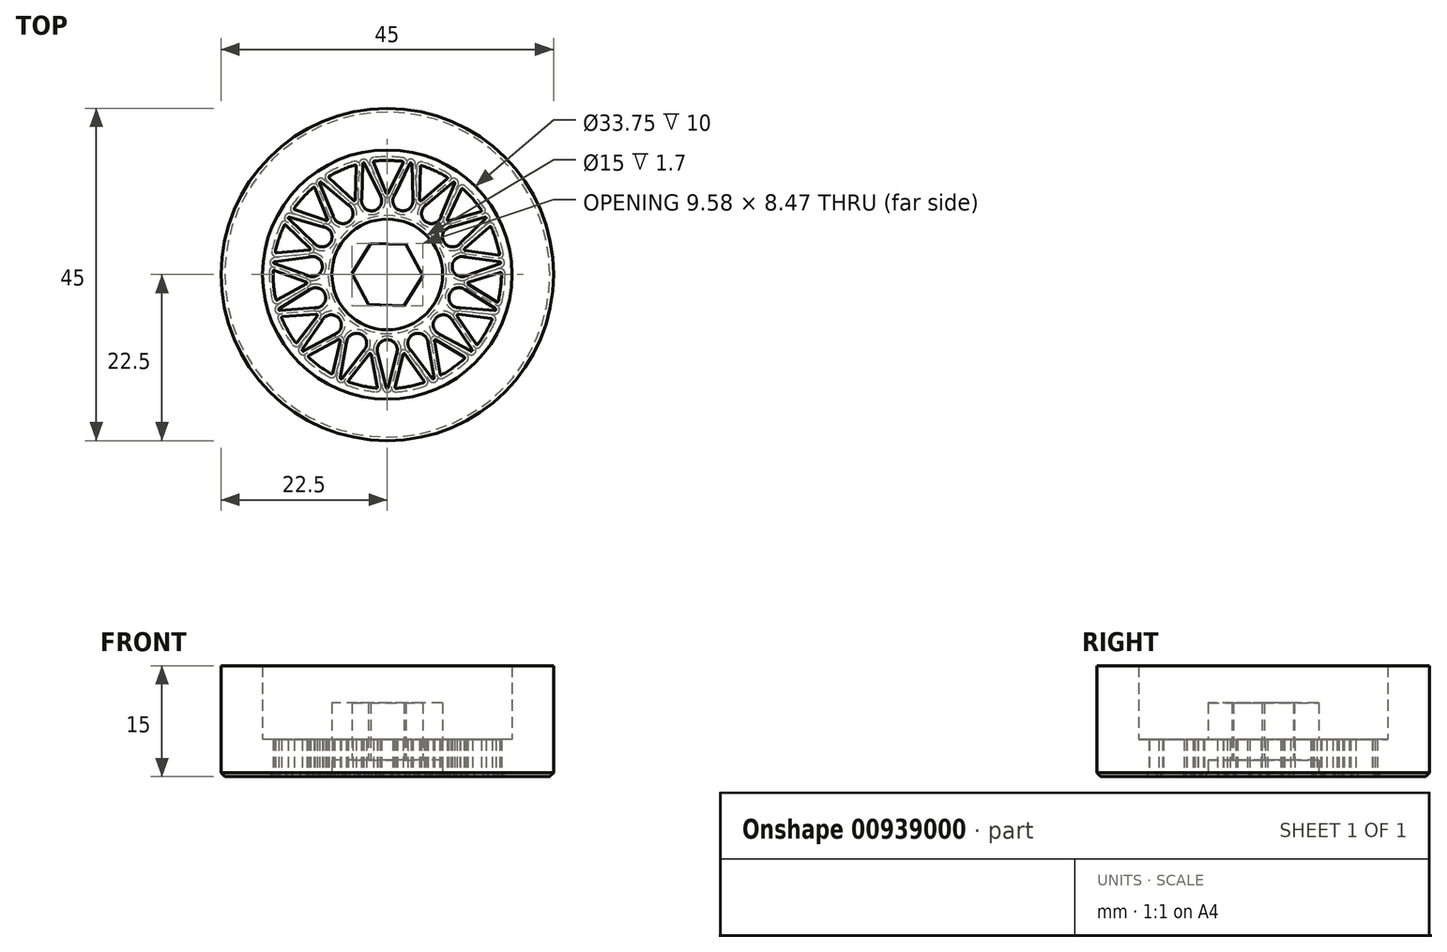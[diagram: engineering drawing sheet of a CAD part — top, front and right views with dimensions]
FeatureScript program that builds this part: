
annotation { "Feature Type Name" : "Feature", "Feature Type Description" : "" }
export const myFeature = defineFeature(function(context is Context, id is Id, definition is map)
    precondition{}
    {
        {
            var Q0;
            Q0=qCreatedBy(makeId("Top.planeOp"),FACE);
            var sketch = newSketch(context, id + "F0", { "sketchPlane" : qUnion([Q0])});
            skCircle(sketch, "E0", {"center": v(0, 0) * mm, "radius": 22.5 * mm});
            skCircle(sketch, "E1", {"center": v(0, 0) * mm, "radius": 16.88 * mm});
            skCircle(sketch, "E2", {"center": v(0, 0) * mm, "radius": 7.5 * mm});
            skCircle(sketch, "E3", {"center": v(0, 0) * mm, "radius": 15.9 * mm, "construction": true});
            skCircle(sketch, "E4", {"center": v(0, 0) * mm, "radius": 5.66 * mm, "construction": true});
            skLineSegment(sketch, "E5", {"start": v(0, -5.66) * mm, "end": v(0, -15.9) * mm, "construction": true});
            skArc(sketch, "E6", {"start": v(1.26, -10.71) * mm, "mid": v(0, -8.84) * mm, "end": v(-1.26, -10.71) * mm});
            skLineSegment(sketch, "E7", {"start": v(-1.26, -10.71) * mm, "end": v(-0.14, -15.34) * mm});
            skLineSegment(sketch, "E8", {"start": v(0.14, -15.34) * mm, "end": v(1.26, -10.71) * mm});
            skPoint(sketch, "E9.visualSharp", {"position": v(0, -15.9) * mm});
            skArc(sketch, "E9.filletArc", {"start": v(-0.14, -15.34) * mm, "mid": v(0, -15.44) * mm, "end": v(0.14, -15.34) * mm});
            skArc(sketch, "E10.1.0", {"start": v(5.51, -9.27) * mm, "mid": v(3.6, -8.07) * mm, "end": v(3.2, -10.3) * mm});
            skLineSegment(sketch, "E10.1.1", {"start": v(6.36, -13.95) * mm, "end": v(5.51, -9.27) * mm});
            skLineSegment(sketch, "E10.1.2", {"start": v(3.2, -10.3) * mm, "end": v(6.11, -14.07) * mm});
            skArc(sketch, "E10.1.3", {"start": v(6.11, -14.07) * mm, "mid": v(6.28, -14.1) * mm, "end": v(6.36, -13.95) * mm});
            skArc(sketch, "E10.2.0", {"start": v(8.8, -6.23) * mm, "mid": v(6.57, -5.91) * mm, "end": v(7.12, -8.1) * mm});
            skLineSegment(sketch, "E10.2.1", {"start": v(11.49, -10.16) * mm, "end": v(8.8, -6.23) * mm});
            skLineSegment(sketch, "E10.2.2", {"start": v(7.12, -8.1) * mm, "end": v(11.3, -10.36) * mm});
            skArc(sketch, "E10.2.3", {"start": v(11.3, -10.36) * mm, "mid": v(11.48, -10.33) * mm, "end": v(11.49, -10.16) * mm});
            skArc(sketch, "E10.3.0", {"start": v(10.58, -2.1) * mm, "mid": v(8.4, -2.73) * mm, "end": v(9.8, -4.51) * mm});
            skLineSegment(sketch, "E10.3.1", {"start": v(14.63, -4.6) * mm, "end": v(10.58, -2.1) * mm});
            skLineSegment(sketch, "E10.3.2", {"start": v(9.8, -4.51) * mm, "end": v(14.54, -4.87) * mm});
            skArc(sketch, "E10.3.3", {"start": v(14.54, -4.87) * mm, "mid": v(14.69, -4.77) * mm, "end": v(14.63, -4.6) * mm});
            skArc(sketch, "E10.4.0", {"start": v(10.52, 2.38) * mm, "mid": v(8.79, 0.92) * mm, "end": v(10.79, -0.14) * mm});
            skLineSegment(sketch, "E10.4.1", {"start": v(15.24, 1.74) * mm, "end": v(10.52, 2.38) * mm});
            skLineSegment(sketch, "E10.4.2", {"start": v(10.79, -0.14) * mm, "end": v(15.27, 1.47) * mm});
            skArc(sketch, "E10.4.3", {"start": v(15.27, 1.47) * mm, "mid": v(15.36, 1.61) * mm, "end": v(15.24, 1.74) * mm});
            skArc(sketch, "E10.5.0", {"start": v(8.65, 6.45) * mm, "mid": v(7.65, 4.42) * mm, "end": v(9.9, 4.26) * mm});
            skLineSegment(sketch, "E10.5.1", {"start": v(13.21, 7.79) * mm, "end": v(8.65, 6.45) * mm});
            skLineSegment(sketch, "E10.5.2", {"start": v(9.9, 4.26) * mm, "end": v(13.35, 7.55) * mm});
            skArc(sketch, "E10.5.3", {"start": v(13.35, 7.55) * mm, "mid": v(13.38, 7.72) * mm, "end": v(13.21, 7.79) * mm});
            skArc(sketch, "E10.6.0", {"start": v(5.27, 9.4) * mm, "mid": v(5.2, 7.15) * mm, "end": v(7.32, 7.92) * mm});
            skLineSegment(sketch, "E10.6.1", {"start": v(8.9, 12.49) * mm, "end": v(5.27, 9.4) * mm});
            skLineSegment(sketch, "E10.6.2", {"start": v(7.32, 7.92) * mm, "end": v(9.13, 12.33) * mm});
            skArc(sketch, "E10.6.3", {"start": v(9.13, 12.33) * mm, "mid": v(9.08, 12.5) * mm, "end": v(8.9, 12.49) * mm});
            skArc(sketch, "E10.7.0", {"start": v(1, 10.74) * mm, "mid": v(1.84, 8.64) * mm, "end": v(3.46, 10.22) * mm});
            skLineSegment(sketch, "E10.7.1", {"start": v(3.05, 15.03) * mm, "end": v(1, 10.74) * mm});
            skLineSegment(sketch, "E10.7.2", {"start": v(3.46, 10.22) * mm, "end": v(3.32, 14.97) * mm});
            skArc(sketch, "E10.7.3", {"start": v(3.32, 14.97) * mm, "mid": v(3.21, 15.1) * mm, "end": v(3.05, 15.03) * mm});
            skArc(sketch, "E10.8.0", {"start": v(-3.46, 10.22) * mm, "mid": v(-1.84, 8.64) * mm, "end": v(-1, 10.74) * mm});
            skLineSegment(sketch, "E10.8.1", {"start": v(-3.32, 14.97) * mm, "end": v(-3.46, 10.22) * mm});
            skLineSegment(sketch, "E10.8.2", {"start": v(-1, 10.74) * mm, "end": v(-3.05, 15.03) * mm});
            skArc(sketch, "E10.8.3", {"start": v(-3.05, 15.03) * mm, "mid": v(-3.21, 15.1) * mm, "end": v(-3.32, 14.97) * mm});
            skArc(sketch, "E10.9.0", {"start": v(-7.32, 7.92) * mm, "mid": v(-5.2, 7.15) * mm, "end": v(-5.27, 9.4) * mm});
            skLineSegment(sketch, "E10.9.1", {"start": v(-9.13, 12.33) * mm, "end": v(-7.32, 7.92) * mm});
            skLineSegment(sketch, "E10.9.2", {"start": v(-5.27, 9.4) * mm, "end": v(-8.9, 12.49) * mm});
            skArc(sketch, "E10.9.3", {"start": v(-8.9, 12.49) * mm, "mid": v(-9.08, 12.5) * mm, "end": v(-9.13, 12.33) * mm});
            skArc(sketch, "E10.10.0", {"start": v(-9.9, 4.26) * mm, "mid": v(-7.65, 4.42) * mm, "end": v(-8.65, 6.45) * mm});
            skLineSegment(sketch, "E10.10.1", {"start": v(-13.35, 7.55) * mm, "end": v(-9.9, 4.26) * mm});
            skLineSegment(sketch, "E10.10.2", {"start": v(-8.65, 6.45) * mm, "end": v(-13.21, 7.79) * mm});
            skArc(sketch, "E10.10.3", {"start": v(-13.21, 7.79) * mm, "mid": v(-13.38, 7.72) * mm, "end": v(-13.35, 7.55) * mm});
            skArc(sketch, "E10.11.0", {"start": v(-10.79, -0.14) * mm, "mid": v(-8.79, 0.92) * mm, "end": v(-10.52, 2.38) * mm});
            skLineSegment(sketch, "E10.11.1", {"start": v(-15.27, 1.47) * mm, "end": v(-10.79, -0.14) * mm});
            skLineSegment(sketch, "E10.11.2", {"start": v(-10.52, 2.38) * mm, "end": v(-15.24, 1.74) * mm});
            skArc(sketch, "E10.11.3", {"start": v(-15.24, 1.74) * mm, "mid": v(-15.36, 1.61) * mm, "end": v(-15.27, 1.47) * mm});
            skArc(sketch, "E10.12.0", {"start": v(-9.8, -4.51) * mm, "mid": v(-8.4, -2.73) * mm, "end": v(-10.58, -2.1) * mm});
            skLineSegment(sketch, "E10.12.1", {"start": v(-14.54, -4.87) * mm, "end": v(-9.8, -4.51) * mm});
            skLineSegment(sketch, "E10.12.2", {"start": v(-10.58, -2.1) * mm, "end": v(-14.63, -4.6) * mm});
            skArc(sketch, "E10.12.3", {"start": v(-14.63, -4.6) * mm, "mid": v(-14.69, -4.77) * mm, "end": v(-14.54, -4.87) * mm});
            skArc(sketch, "E10.13.0", {"start": v(-7.12, -8.1) * mm, "mid": v(-6.57, -5.91) * mm, "end": v(-8.8, -6.23) * mm});
            skLineSegment(sketch, "E10.13.1", {"start": v(-11.3, -10.36) * mm, "end": v(-7.12, -8.1) * mm});
            skLineSegment(sketch, "E10.13.2", {"start": v(-8.8, -6.23) * mm, "end": v(-11.49, -10.16) * mm});
            skArc(sketch, "E10.13.3", {"start": v(-11.49, -10.16) * mm, "mid": v(-11.48, -10.33) * mm, "end": v(-11.3, -10.36) * mm});
            skArc(sketch, "E10.14.0", {"start": v(-3.2, -10.3) * mm, "mid": v(-3.6, -8.07) * mm, "end": v(-5.51, -9.27) * mm});
            skLineSegment(sketch, "E10.14.1", {"start": v(-6.11, -14.07) * mm, "end": v(-3.2, -10.3) * mm});
            skLineSegment(sketch, "E10.14.2", {"start": v(-5.51, -9.27) * mm, "end": v(-6.36, -13.95) * mm});
            skArc(sketch, "E10.14.3", {"start": v(-6.36, -13.95) * mm, "mid": v(-6.28, -14.1) * mm, "end": v(-6.11, -14.07) * mm});
            skCircle(sketch, "E11", {"center": v(0, 0) * mm, "radius": 15.46 * mm, "construction": true});
            skPoint(sketch, "E12", {"position": v(-5.37, -14.5) * mm});
            skPoint(sketch, "E13", {"position": v(-1.3, -15.4) * mm});
            skArc(sketch, "E14", {"start": v(-5.18, -14.57) * mm, "mid": v(-3.35, -15.08) * mm, "end": v(-1.48, -15.39) * mm});
            skLineSegment(sketch, "E15", {"start": v(-3.2, -10.3) * mm, "end": v(-1.26, -10.71) * mm, "construction": true});
            skLineSegment(sketch, "E16", {"start": v(-5.25, -14.34) * mm, "end": v(-2.43, -10.75) * mm});
            skLineSegment(sketch, "E17", {"start": v(-2.17, -10.81) * mm, "end": v(-1.33, -15.22) * mm});
            skArc(sketch, "E18.filletArc", {"start": v(-5.25, -14.34) * mm, "mid": v(-5.27, -14.47) * mm, "end": v(-5.18, -14.57) * mm});
            skArc(sketch, "E19.filletArc", {"start": v(-1.48, -15.39) * mm, "mid": v(-1.36, -15.34) * mm, "end": v(-1.33, -15.22) * mm});
            skPoint(sketch, "E20.visualSharp", {"position": v(-2.23, -10.5) * mm});
            skArc(sketch, "E20.filletArc", {"start": v(-2.17, -10.81) * mm, "mid": v(-2.28, -10.7) * mm, "end": v(-2.43, -10.75) * mm});
            skArc(sketch, "E21.1.0", {"start": v(1.2, -15.41) * mm, "mid": v(3.07, -15.14) * mm, "end": v(4.9, -14.66) * mm});
            skLineSegment(sketch, "E21.1.1", {"start": v(2.41, -10.76) * mm, "end": v(4.98, -14.44) * mm});
            skLineSegment(sketch, "E21.1.2", {"start": v(1.04, -15.24) * mm, "end": v(2.16, -10.8) * mm});
            skArc(sketch, "E21.1.3", {"start": v(2.41, -10.76) * mm, "mid": v(2.27, -10.7) * mm, "end": v(2.16, -10.8) * mm});
            skArc(sketch, "E21.1.4", {"start": v(4.9, -14.66) * mm, "mid": v(5, -14.57) * mm, "end": v(4.98, -14.44) * mm});
            skArc(sketch, "E21.1.5", {"start": v(1.04, -15.24) * mm, "mid": v(1.07, -15.36) * mm, "end": v(1.2, -15.41) * mm});
            skArc(sketch, "E21.2.0", {"start": v(7.36, -13.6) * mm, "mid": v(8.96, -12.58) * mm, "end": v(10.45, -11.4) * mm});
            skLineSegment(sketch, "E21.2.1", {"start": v(6.58, -8.85) * mm, "end": v(10.42, -11.17) * mm});
            skLineSegment(sketch, "E21.2.2", {"start": v(7.15, -13.5) * mm, "end": v(6.37, -9) * mm});
            skArc(sketch, "E21.2.3", {"start": v(6.58, -8.85) * mm, "mid": v(6.43, -8.86) * mm, "end": v(6.37, -9) * mm});
            skArc(sketch, "E21.2.4", {"start": v(10.45, -11.4) * mm, "mid": v(10.5, -11.28) * mm, "end": v(10.42, -11.17) * mm});
            skArc(sketch, "E21.2.5", {"start": v(7.15, -13.5) * mm, "mid": v(7.23, -13.6) * mm, "end": v(7.36, -13.6) * mm});
            skArc(sketch, "E21.3.0", {"start": v(12.25, -9.43) * mm, "mid": v(13.3, -7.85) * mm, "end": v(14.18, -6.16) * mm});
            skLineSegment(sketch, "E21.3.1", {"start": v(9.61, -5.4) * mm, "end": v(14.07, -5.96) * mm});
            skLineSegment(sketch, "E21.3.2", {"start": v(12.02, -9.42) * mm, "end": v(9.48, -5.63) * mm});
            skArc(sketch, "E21.3.3", {"start": v(9.61, -5.4) * mm, "mid": v(9.47, -5.48) * mm, "end": v(9.48, -5.63) * mm});
            skArc(sketch, "E21.3.4", {"start": v(14.18, -6.16) * mm, "mid": v(14.17, -6.04) * mm, "end": v(14.07, -5.96) * mm});
            skArc(sketch, "E21.3.5", {"start": v(12.02, -9.42) * mm, "mid": v(12.14, -9.48) * mm, "end": v(12.25, -9.43) * mm});
            skArc(sketch, "E21.4.0", {"start": v(15.03, -3.63) * mm, "mid": v(15.35, -1.76) * mm, "end": v(15.46, 0.14) * mm});
            skLineSegment(sketch, "E21.4.1", {"start": v(10.98, -1.03) * mm, "end": v(15.28, 0.27) * mm});
            skLineSegment(sketch, "E21.4.2", {"start": v(14.81, -3.72) * mm, "end": v(10.95, -1.29) * mm});
            skArc(sketch, "E21.4.3", {"start": v(10.98, -1.03) * mm, "mid": v(10.88, -1.15) * mm, "end": v(10.95, -1.29) * mm});
            skArc(sketch, "E21.4.4", {"start": v(15.46, 0.14) * mm, "mid": v(15.4, 0.25) * mm, "end": v(15.28, 0.27) * mm});
            skArc(sketch, "E21.4.5", {"start": v(14.81, -3.72) * mm, "mid": v(14.94, -3.73) * mm, "end": v(15.03, -3.63) * mm});
            skArc(sketch, "E21.5.0", {"start": v(15.2, 2.8) * mm, "mid": v(14.74, 4.64) * mm, "end": v(14.07, 6.41) * mm});
            skLineSegment(sketch, "E21.5.1", {"start": v(10.45, 3.52) * mm, "end": v(13.84, 6.46) * mm});
            skLineSegment(sketch, "E21.5.2", {"start": v(15.05, 2.63) * mm, "end": v(10.52, 3.28) * mm});
            skArc(sketch, "E21.5.3", {"start": v(10.45, 3.52) * mm, "mid": v(10.4, 3.38) * mm, "end": v(10.52, 3.28) * mm});
            skArc(sketch, "E21.5.4", {"start": v(14.07, 6.41) * mm, "mid": v(13.97, 6.5) * mm, "end": v(13.84, 6.46) * mm});
            skArc(sketch, "E21.5.5", {"start": v(15.05, 2.63) * mm, "mid": v(15.17, 2.67) * mm, "end": v(15.2, 2.8) * mm});
            skArc(sketch, "E21.6.0", {"start": v(12.75, 8.74) * mm, "mid": v(11.58, 10.23) * mm, "end": v(10.24, 11.58) * mm});
            skLineSegment(sketch, "E21.6.1", {"start": v(8.11, 7.47) * mm, "end": v(10.02, 11.53) * mm});
            skLineSegment(sketch, "E21.6.2", {"start": v(12.68, 8.52) * mm, "end": v(8.28, 7.27) * mm});
            skArc(sketch, "E21.6.3", {"start": v(8.11, 7.47) * mm, "mid": v(8.13, 7.32) * mm, "end": v(8.28, 7.27) * mm});
            skArc(sketch, "E21.6.4", {"start": v(10.24, 11.58) * mm, "mid": v(10.12, 11.61) * mm, "end": v(10.02, 11.53) * mm});
            skArc(sketch, "E21.6.5", {"start": v(12.68, 8.52) * mm, "mid": v(12.77, 8.61) * mm, "end": v(12.75, 8.74) * mm});
            skArc(sketch, "E21.7.0", {"start": v(8.1, 13.17) * mm, "mid": v(6.42, 14.06) * mm, "end": v(4.65, 14.75) * mm});
            skLineSegment(sketch, "E21.7.1", {"start": v(4.37, 10.12) * mm, "end": v(4.46, 14.61) * mm});
            skLineSegment(sketch, "E21.7.2", {"start": v(8.11, 12.94) * mm, "end": v(4.6, 10.01) * mm});
            skArc(sketch, "E21.7.3", {"start": v(4.37, 10.12) * mm, "mid": v(4.46, 10) * mm, "end": v(4.6, 10.01) * mm});
            skArc(sketch, "E21.7.4", {"start": v(4.65, 14.75) * mm, "mid": v(4.52, 14.73) * mm, "end": v(4.46, 14.61) * mm});
            skArc(sketch, "E21.7.5", {"start": v(8.11, 12.94) * mm, "mid": v(8.16, 13.06) * mm, "end": v(8.1, 13.17) * mm});
            skArc(sketch, "E21.8.0", {"start": v(2.04, 15.33) * mm, "mid": v(0.14, 15.45) * mm, "end": v(-1.75, 15.36) * mm});
            skLineSegment(sketch, "E21.8.1", {"start": v(-0.12, 11.03) * mm, "end": v(-1.87, 15.16) * mm});
            skLineSegment(sketch, "E21.8.2", {"start": v(2.15, 15.12) * mm, "end": v(0.14, 11.02) * mm});
            skArc(sketch, "E21.8.3", {"start": v(-0.12, 11.03) * mm, "mid": v(0, 10.94) * mm, "end": v(0.14, 11.02) * mm});
            skArc(sketch, "E21.8.4", {"start": v(-1.75, 15.36) * mm, "mid": v(-1.86, 15.3) * mm, "end": v(-1.87, 15.16) * mm});
            skArc(sketch, "E21.8.5", {"start": v(2.15, 15.12) * mm, "mid": v(2.15, 15.25) * mm, "end": v(2.04, 15.33) * mm});
            skArc(sketch, "E21.9.0", {"start": v(-4.37, 14.83) * mm, "mid": v(-6.15, 14.17) * mm, "end": v(-7.85, 13.32) * mm});
            skLineSegment(sketch, "E21.9.1", {"start": v(-4.6, 10.03) * mm, "end": v(-7.87, 13.1) * mm});
            skLineSegment(sketch, "E21.9.2", {"start": v(-4.19, 14.69) * mm, "end": v(-4.36, 10.12) * mm});
            skArc(sketch, "E21.9.3", {"start": v(-4.6, 10.03) * mm, "mid": v(-4.45, 10) * mm, "end": v(-4.36, 10.12) * mm});
            skArc(sketch, "E21.9.4", {"start": v(-7.85, 13.32) * mm, "mid": v(-7.92, 13.21) * mm, "end": v(-7.87, 13.1) * mm});
            skArc(sketch, "E21.9.5", {"start": v(-4.19, 14.69) * mm, "mid": v(-4.24, 14.8) * mm, "end": v(-4.37, 14.83) * mm});
            skArc(sketch, "E21.10.0", {"start": v(-10.03, 11.77) * mm, "mid": v(-11.38, 10.45) * mm, "end": v(-12.59, 8.98) * mm});
            skLineSegment(sketch, "E21.10.1", {"start": v(-8.28, 7.29) * mm, "end": v(-12.52, 8.76) * mm});
            skLineSegment(sketch, "E21.10.2", {"start": v(-9.8, 11.72) * mm, "end": v(-8.1, 7.48) * mm});
            skArc(sketch, "E21.10.3", {"start": v(-8.28, 7.29) * mm, "mid": v(-8.13, 7.33) * mm, "end": v(-8.1, 7.48) * mm});
            skArc(sketch, "E21.10.4", {"start": v(-12.59, 8.98) * mm, "mid": v(-12.6, 8.85) * mm, "end": v(-12.52, 8.76) * mm});
            skArc(sketch, "E21.10.5", {"start": v(-9.8, 11.72) * mm, "mid": v(-9.9, 11.8) * mm, "end": v(-10.03, 11.77) * mm});
            skArc(sketch, "E21.11.0", {"start": v(-13.95, 6.67) * mm, "mid": v(-14.65, 4.91) * mm, "end": v(-15.15, 3.08) * mm});
            skLineSegment(sketch, "E21.11.1", {"start": v(-10.53, 3.3) * mm, "end": v(-15, 2.9) * mm});
            skLineSegment(sketch, "E21.11.2", {"start": v(-13.72, 6.72) * mm, "end": v(-10.44, 3.54) * mm});
            skArc(sketch, "E21.11.3", {"start": v(-10.53, 3.3) * mm, "mid": v(-10.4, 3.39) * mm, "end": v(-10.44, 3.54) * mm});
            skArc(sketch, "E21.11.4", {"start": v(-15.15, 3.08) * mm, "mid": v(-15.12, 2.96) * mm, "end": v(-15, 2.9) * mm});
            skArc(sketch, "E21.11.5", {"start": v(-13.72, 6.72) * mm, "mid": v(-13.84, 6.75) * mm, "end": v(-13.95, 6.67) * mm});
            skArc(sketch, "E21.12.0", {"start": v(-15.45, 0.43) * mm, "mid": v(-15.38, -1.47) * mm, "end": v(-15.1, -3.35) * mm});
            skLineSegment(sketch, "E21.12.1", {"start": v(-10.96, -1.27) * mm, "end": v(-14.89, -3.44) * mm});
            skLineSegment(sketch, "E21.12.2", {"start": v(-15.26, 0.56) * mm, "end": v(-10.97, -1.02) * mm});
            skArc(sketch, "E21.12.3", {"start": v(-10.96, -1.27) * mm, "mid": v(-10.88, -1.14) * mm, "end": v(-10.97, -1.02) * mm});
            skArc(sketch, "E21.12.4", {"start": v(-15.1, -3.35) * mm, "mid": v(-15.01, -3.45) * mm, "end": v(-14.89, -3.44) * mm});
            skArc(sketch, "E21.12.5", {"start": v(-15.26, 0.56) * mm, "mid": v(-15.4, 0.54) * mm, "end": v(-15.45, 0.43) * mm});
            skArc(sketch, "E21.13.0", {"start": v(-14.3, -5.9) * mm, "mid": v(-13.45, -7.6) * mm, "end": v(-12.43, -9.2) * mm});
            skLineSegment(sketch, "E21.13.1", {"start": v(-9.5, -5.62) * mm, "end": v(-12.2, -9.2) * mm});
            skLineSegment(sketch, "E21.13.2", {"start": v(-14.17, -5.7) * mm, "end": v(-9.61, -5.4) * mm});
            skArc(sketch, "E21.13.3", {"start": v(-9.5, -5.62) * mm, "mid": v(-9.48, -5.47) * mm, "end": v(-9.61, -5.4) * mm});
            skArc(sketch, "E21.13.4", {"start": v(-12.43, -9.2) * mm, "mid": v(-12.31, -9.26) * mm, "end": v(-12.2, -9.2) * mm});
            skArc(sketch, "E21.13.5", {"start": v(-14.17, -5.7) * mm, "mid": v(-14.28, -5.77) * mm, "end": v(-14.3, -5.9) * mm});
            skArc(sketch, "E21.14.0", {"start": v(-10.66, -11.2) * mm, "mid": v(-9.2, -12.41) * mm, "end": v(-7.61, -13.46) * mm});
            skLineSegment(sketch, "E21.14.1", {"start": v(-6.38, -9) * mm, "end": v(-7.4, -13.37) * mm});
            skLineSegment(sketch, "E21.14.2", {"start": v(-10.63, -10.97) * mm, "end": v(-6.59, -8.84) * mm});
            skArc(sketch, "E21.14.3", {"start": v(-6.38, -9) * mm, "mid": v(-6.44, -8.85) * mm, "end": v(-6.59, -8.84) * mm});
            skArc(sketch, "E21.14.4", {"start": v(-7.61, -13.46) * mm, "mid": v(-7.48, -13.46) * mm, "end": v(-7.4, -13.37) * mm});
            skArc(sketch, "E21.14.5", {"start": v(-10.63, -10.97) * mm, "mid": v(-10.7, -11.08) * mm, "end": v(-10.66, -11.2) * mm});
            skSolve(sketch);
        }
        {
            var Q0;
            Q0=makeQuery(id+"F0.imprint","IMPRINT",FACE,{"disambiguationData":[TD([[makeQuery(id+"F0.imprint","IMPRINT",EDGE,{"derivedFrom":sQuery(id+"F0.wireOp",EDGE,"E0")}),1.0]])]});
            extrude(context, id + "F1", {"entities" : qUnion([Q0]), "depth" : 15 * mm, "offsetDistance" : 25 * mm});
        }
        {
            var Q0;
            Q0=makeQuery(id+"F0.imprint","IMPRINT",FACE,{"disambiguationData":[TD([[makeQuery(id+"F0.imprint","IMPRINT",EDGE,{"derivedFrom":sQuery(id+"F0.wireOp",EDGE,"E1")}),1.0]])]});
            extrude(context, id + "F2", {"entities" : qUnion([Q0]), "operationType" : NewBodyOperationType.ADD, "depth" : 5 * mm, "offsetDistance" : 25 * mm});
        }
        {
            var Q0;
            {var subQ0=sQuery(id+"F0.wireOp",EDGE,"E2");var subQ1=makeQuery(id+"F0.imprint","INTERSECT",VERTEX,{"derivedFrom":[subQ0,sQuery(id+"F0.wireOp",EDGE,"FMw9U3Ag-M4uU-eOUw-AIyu-Y3kzjyrUIhWa.right")]});Q0=makeQuery(id+"F0.imprint","IMPRINT",FACE,{"disambiguationData":[TD([[makeQuery(id+"F0.imprint","IMPRINT",EDGE,{"disambiguationData":[TD([[subQ1,1.0]])],"derivedFrom":subQ0}),1.0]])]});}
            extrude(context, id + "F3", {"entities" : qUnion([Q0]), "operationType" : NewBodyOperationType.ADD, "depth" : 10 * mm, "offsetDistance" : 25 * mm});
        }
        {
            var Q0;
            Q0=makeQuery(id+"F0.imprint","IMPRINT",FACE,{"disambiguationData":[TD([[makeQuery(id+"F0.imprint","IMPRINT",EDGE,{"derivedFrom":sQuery(id+"F0.wireOp",EDGE,"E2")}),1.0]])]});
            extrude(context, id + "F4", {"entities" : qUnion([Q0]), "operationType" : NewBodyOperationType.REMOVE, "depth" : 2.2 * mm, "offsetDistance" : 25 * mm});
        }
        {
            var Q0;
            Q0=makeQuery(id+"F0.imprint","IMPRINT",FACE,{"disambiguationData":[TD([[makeQuery(id+"F0.imprint","IMPRINT",EDGE,{"derivedFrom":sQuery(id+"F0.wireOp",EDGE,"E2")}),1.0]])]});
            var sketch = newSketch(context, id + "F5", { "sketchPlane" : qUnion([Q0])});
            skPoint(sketch, "E22.center", {"position": v(0, 0) * mm});
            skPoint(sketch, "E23.0.midPoint", {"position": v(-3.35, 1.99) * mm});
            skCircle(sketch, "E24.cCircle", {"center": v(0, 0) * mm, "radius": 4.15 * mm, "construction": true});
            skLineSegment(sketch, "E24.0", {"start": v(-4.79, 0.17) * mm, "end": v(-2.25, 4.23) * mm});
            skLineSegment(sketch, "E24.1", {"start": v(-2.25, 4.23) * mm, "end": v(2.54, 4.06) * mm});
            skLineSegment(sketch, "E24.2", {"start": v(2.54, 4.06) * mm, "end": v(4.79, -0.17) * mm});
            skLineSegment(sketch, "E24.3", {"start": v(4.79, -0.17) * mm, "end": v(2.25, -4.23) * mm});
            skLineSegment(sketch, "E24.4", {"start": v(2.25, -4.23) * mm, "end": v(-2.54, -4.06) * mm});
            skLineSegment(sketch, "E24.5", {"start": v(-2.54, -4.06) * mm, "end": v(-4.79, 0.17) * mm});
            skPoint(sketch, "E24.0.midPoint", {"position": v(-3.52, 2.2) * mm});
            skPoint(sketch, "E25.orphan", {"position": v(-2.3, -3.87) * mm});
            skPoint(sketch, "E26.orphan", {"position": v(2.2, -3.92) * mm});
            skPoint(sketch, "E27.orphan", {"position": v(-4.5, 0.05) * mm});
            skPoint(sketch, "E23.1.start.orphan", {"position": v(-2.2, 3.92) * mm});
            skSolve(sketch);
        }
        {
            var Q0;
            Q0=makeQuery(id+"F5.imprint","IMPRINT",FACE,{"disambiguationData":[TD([[makeQuery(id+"F5.imprint","IMPRINT",EDGE,{"derivedFrom":sQuery(id+"F5.wireOp",EDGE,"E24.0")}),-1.0]])]});
            extrude(context, id + "F6", {"entities" : qUnion([Q0]), "operationType" : NewBodyOperationType.REMOVE, "depth" : 25 * mm, "offsetDistance" : 25 * mm});
        }
        {
            var Q0;
            {var subQ0=sQuery(id+"F0.wireOp",EDGE,"E2");var subQ1=sQuery(id+"F0.wireOp",EDGE,"E1");Q0=makeQuery(id+"F3.boolean.opBoolean","MERGE",FACE,{"derivedFrom":[makeQuery(id+"F2.boolean.opBoolean","MERGE",FACE,{"derivedFrom":[makeQuery(id+"F1.opExtrude","CAP_FACE",FACE,{"disambiguationData":[OSD([sQuery(id+"F0.wireOp",EDGE,"E0"),subQ1])],"isStart":true}),makeQuery(id+"F2.opExtrude","CAP_FACE",FACE,{"disambiguationData":[OSD([subQ1,subQ0,sQuery(id+"F0.wireOp",EDGE,"l7tfmqop-6kv4-bzPA-Ropg-I9eWoZhItPkr"),sQuery(id+"F0.wireOp",EDGE,"YxJzRuay-E9xs-sZhK-4W0r-wAjnjXR5L8FN"),sQuery(id+"F0.wireOp",EDGE,"PMRRlQ6P-4Bp1-SP5u-pO5f-w0NEBdmSjVl4"),sQuery(id+"F0.wireOp",EDGE,"69a66aeb-96e8-4236-adc5-40ebd95f15ce.filletArc"),sQuery(id+"F0.wireOp",EDGE,"1d552ee7-da9b-4f0c-a288-42d00aae1e59.1.0"),sQuery(id+"F0.wireOp",EDGE,"1d552ee7-da9b-4f0c-a288-42d00aae1e59.1.1"),sQuery(id+"F0.wireOp",EDGE,"1d552ee7-da9b-4f0c-a288-42d00aae1e59.1.2"),sQuery(id+"F0.wireOp",EDGE,"1d552ee7-da9b-4f0c-a288-42d00aae1e59.1.3"),sQuery(id+"F0.wireOp",EDGE,"1d552ee7-da9b-4f0c-a288-42d00aae1e59.2.0"),sQuery(id+"F0.wireOp",EDGE,"1d552ee7-da9b-4f0c-a288-42d00aae1e59.2.1"),sQuery(id+"F0.wireOp",EDGE,"1d552ee7-da9b-4f0c-a288-42d00aae1e59.2.2"),sQuery(id+"F0.wireOp",EDGE,"1d552ee7-da9b-4f0c-a288-42d00aae1e59.2.3"),sQuery(id+"F0.wireOp",EDGE,"1d552ee7-da9b-4f0c-a288-42d00aae1e59.3.0"),sQuery(id+"F0.wireOp",EDGE,"1d552ee7-da9b-4f0c-a288-42d00aae1e59.3.1"),sQuery(id+"F0.wireOp",EDGE,"1d552ee7-da9b-4f0c-a288-42d00aae1e59.3.2"),sQuery(id+"F0.wireOp",EDGE,"1d552ee7-da9b-4f0c-a288-42d00aae1e59.3.3"),sQuery(id+"F0.wireOp",EDGE,"1d552ee7-da9b-4f0c-a288-42d00aae1e59.4.0"),sQuery(id+"F0.wireOp",EDGE,"1d552ee7-da9b-4f0c-a288-42d00aae1e59.4.1"),sQuery(id+"F0.wireOp",EDGE,"1d552ee7-da9b-4f0c-a288-42d00aae1e59.4.2"),sQuery(id+"F0.wireOp",EDGE,"1d552ee7-da9b-4f0c-a288-42d00aae1e59.4.3"),sQuery(id+"F0.wireOp",EDGE,"1d552ee7-da9b-4f0c-a288-42d00aae1e59.5.0"),sQuery(id+"F0.wireOp",EDGE,"1d552ee7-da9b-4f0c-a288-42d00aae1e59.5.1"),sQuery(id+"F0.wireOp",EDGE,"1d552ee7-da9b-4f0c-a288-42d00aae1e59.5.2"),sQuery(id+"F0.wireOp",EDGE,"1d552ee7-da9b-4f0c-a288-42d00aae1e59.5.3"),sQuery(id+"F0.wireOp",EDGE,"1d552ee7-da9b-4f0c-a288-42d00aae1e59.6.0"),sQuery(id+"F0.wireOp",EDGE,"1d552ee7-da9b-4f0c-a288-42d00aae1e59.6.1"),sQuery(id+"F0.wireOp",EDGE,"1d552ee7-da9b-4f0c-a288-42d00aae1e59.6.2"),sQuery(id+"F0.wireOp",EDGE,"1d552ee7-da9b-4f0c-a288-42d00aae1e59.6.3"),sQuery(id+"F0.wireOp",EDGE,"1d552ee7-da9b-4f0c-a288-42d00aae1e59.7.0"),sQuery(id+"F0.wireOp",EDGE,"1d552ee7-da9b-4f0c-a288-42d00aae1e59.7.1"),sQuery(id+"F0.wireOp",EDGE,"1d552ee7-da9b-4f0c-a288-42d00aae1e59.7.2"),sQuery(id+"F0.wireOp",EDGE,"1d552ee7-da9b-4f0c-a288-42d00aae1e59.7.3"),sQuery(id+"F0.wireOp",EDGE,"1d552ee7-da9b-4f0c-a288-42d00aae1e59.8.0"),sQuery(id+"F0.wireOp",EDGE,"1d552ee7-da9b-4f0c-a288-42d00aae1e59.8.1"),sQuery(id+"F0.wireOp",EDGE,"1d552ee7-da9b-4f0c-a288-42d00aae1e59.8.2"),sQuery(id+"F0.wireOp",EDGE,"1d552ee7-da9b-4f0c-a288-42d00aae1e59.8.3"),sQuery(id+"F0.wireOp",EDGE,"1d552ee7-da9b-4f0c-a288-42d00aae1e59.9.0"),sQuery(id+"F0.wireOp",EDGE,"1d552ee7-da9b-4f0c-a288-42d00aae1e59.9.1"),sQuery(id+"F0.wireOp",EDGE,"1d552ee7-da9b-4f0c-a288-42d00aae1e59.9.2"),sQuery(id+"F0.wireOp",EDGE,"1d552ee7-da9b-4f0c-a288-42d00aae1e59.9.3"),sQuery(id+"F0.wireOp",EDGE,"dG9ruqm5-QT7Y-QHdv-tEC1-1vZ8V0C7jhKi"),sQuery(id+"F0.wireOp",EDGE,"13zynFo3-rpzZ-Hc7Q-yODg-0hWWHLczEeh4"),sQuery(id+"F0.wireOp",EDGE,"LefVzuDw-nWrM-VCjd-qSRF-Sznb41wakj4H"),sQuery(id+"F0.wireOp",EDGE,"FdDrVg9r-qZOv-yWwV-fWKn-j6eQ8j2AcD15"),sQuery(id+"F0.wireOp",EDGE,"9baecae1-cf54-4927-a911-c9c189e9ac7c.1.0"),sQuery(id+"F0.wireOp",EDGE,"9baecae1-cf54-4927-a911-c9c189e9ac7c.1.1"),sQuery(id+"F0.wireOp",EDGE,"9baecae1-cf54-4927-a911-c9c189e9ac7c.1.2"),sQuery(id+"F0.wireOp",EDGE,"9baecae1-cf54-4927-a911-c9c189e9ac7c.1.3"),sQuery(id+"F0.wireOp",EDGE,"9baecae1-cf54-4927-a911-c9c189e9ac7c.2.0"),sQuery(id+"F0.wireOp",EDGE,"9baecae1-cf54-4927-a911-c9c189e9ac7c.2.1"),sQuery(id+"F0.wireOp",EDGE,"9baecae1-cf54-4927-a911-c9c189e9ac7c.2.2"),sQuery(id+"F0.wireOp",EDGE,"9baecae1-cf54-4927-a911-c9c189e9ac7c.2.3"),sQuery(id+"F0.wireOp",EDGE,"9baecae1-cf54-4927-a911-c9c189e9ac7c.3.0"),sQuery(id+"F0.wireOp",EDGE,"9baecae1-cf54-4927-a911-c9c189e9ac7c.3.1"),sQuery(id+"F0.wireOp",EDGE,"9baecae1-cf54-4927-a911-c9c189e9ac7c.3.2"),sQuery(id+"F0.wireOp",EDGE,"9baecae1-cf54-4927-a911-c9c189e9ac7c.3.3"),sQuery(id+"F0.wireOp",EDGE,"9baecae1-cf54-4927-a911-c9c189e9ac7c.4.0"),sQuery(id+"F0.wireOp",EDGE,"9baecae1-cf54-4927-a911-c9c189e9ac7c.4.1"),sQuery(id+"F0.wireOp",EDGE,"9baecae1-cf54-4927-a911-c9c189e9ac7c.4.2"),sQuery(id+"F0.wireOp",EDGE,"9baecae1-cf54-4927-a911-c9c189e9ac7c.4.3"),sQuery(id+"F0.wireOp",EDGE,"9baecae1-cf54-4927-a911-c9c189e9ac7c.5.0"),sQuery(id+"F0.wireOp",EDGE,"9baecae1-cf54-4927-a911-c9c189e9ac7c.5.1"),sQuery(id+"F0.wireOp",EDGE,"9baecae1-cf54-4927-a911-c9c189e9ac7c.5.2"),sQuery(id+"F0.wireOp",EDGE,"9baecae1-cf54-4927-a911-c9c189e9ac7c.5.3"),sQuery(id+"F0.wireOp",EDGE,"9baecae1-cf54-4927-a911-c9c189e9ac7c.6.0"),sQuery(id+"F0.wireOp",EDGE,"9baecae1-cf54-4927-a911-c9c189e9ac7c.6.1"),sQuery(id+"F0.wireOp",EDGE,"9baecae1-cf54-4927-a911-c9c189e9ac7c.6.2"),sQuery(id+"F0.wireOp",EDGE,"9baecae1-cf54-4927-a911-c9c189e9ac7c.6.3"),sQuery(id+"F0.wireOp",EDGE,"9baecae1-cf54-4927-a911-c9c189e9ac7c.7.0"),sQuery(id+"F0.wireOp",EDGE,"9baecae1-cf54-4927-a911-c9c189e9ac7c.7.1"),sQuery(id+"F0.wireOp",EDGE,"9baecae1-cf54-4927-a911-c9c189e9ac7c.7.2"),sQuery(id+"F0.wireOp",EDGE,"9baecae1-cf54-4927-a911-c9c189e9ac7c.7.3"),sQuery(id+"F0.wireOp",EDGE,"9baecae1-cf54-4927-a911-c9c189e9ac7c.8.0"),sQuery(id+"F0.wireOp",EDGE,"9baecae1-cf54-4927-a911-c9c189e9ac7c.8.1"),sQuery(id+"F0.wireOp",EDGE,"9baecae1-cf54-4927-a911-c9c189e9ac7c.8.2"),sQuery(id+"F0.wireOp",EDGE,"9baecae1-cf54-4927-a911-c9c189e9ac7c.8.3"),sQuery(id+"F0.wireOp",EDGE,"9baecae1-cf54-4927-a911-c9c189e9ac7c.9.0"),sQuery(id+"F0.wireOp",EDGE,"9baecae1-cf54-4927-a911-c9c189e9ac7c.9.1"),sQuery(id+"F0.wireOp",EDGE,"9baecae1-cf54-4927-a911-c9c189e9ac7c.9.2"),sQuery(id+"F0.wireOp",EDGE,"9baecae1-cf54-4927-a911-c9c189e9ac7c.9.3")])],"isStart":true})]}),makeQuery(id+"F3.opExtrude","CAP_FACE",FACE,{"disambiguationData":[OSD([subQ0])],"isStart":true})]});}
            chamfer(context, id + "F7", {"entities" : qUnion([Q0]), "width" : .5 * mm, "tangentPropagation" : true});
        }
    });
